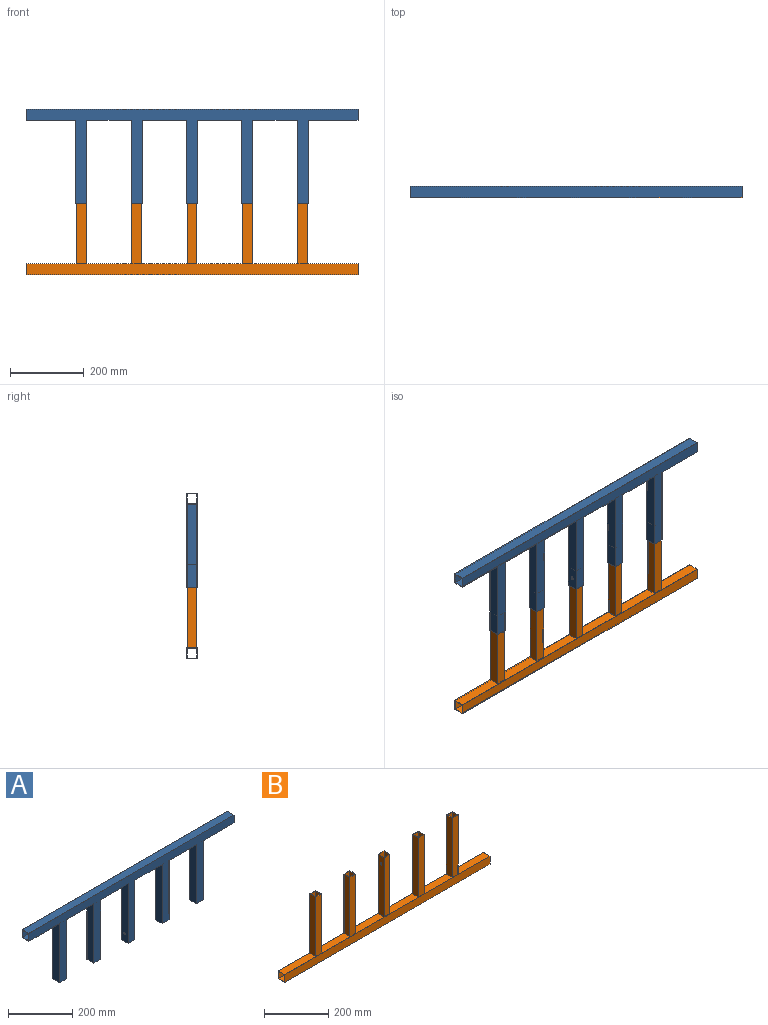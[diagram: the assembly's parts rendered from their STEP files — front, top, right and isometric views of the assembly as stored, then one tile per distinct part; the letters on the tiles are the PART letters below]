
ASSEMBLY  parts=2 mates=1
PART A: 57 faces, bbox 900x30x255 mm
  f0: plane 120x30mm, normal (0,0,-1), area 3600mm2, adj f13,f14,f39,f52
  f1: plane 135x30mm, normal (0,0,-1), area 4050mm2, adj f9,f13,f14,f47
  f2: plane 120x30mm, normal (0,0,-1), area 3600mm2, adj f13,f14,f15,f44
  f3: plane 120x30mm, normal (0,0,-1), area 3600mm2, adj f13,f14,f23,f36
  f4: plane 120x30mm, normal (0,0,-1), area 3600mm2, adj f13,f14,f20,f31
  f5: plane 135x30mm, normal (0,0,-1), area 4050mm2, adj f6,f13,f14,f28
  f6: plane 30x30mm, normal (1,0,0), area 224mm2, adj f5,f7,f8,f10,f11,f12,f13,f14
  f7: plane 900x26mm, normal (0,-1,0), area 23400mm2, adj f6,f9,f10,f11
  f8: plane 900x30mm, normal (0,0,1), area 27000mm2, adj f6,f9,f13,f14
  f9: plane 30x30mm, normal (-1,0,0), area 224mm2, adj f1,f7,f8,f10,f11,f12,f13,f14
  f10: plane 900x26mm, normal (0,0,1), area 23400mm2, adj f6,f7,f9,f12
  f11: plane 900x26mm, normal (0,0,-1), area 23400mm2, adj f6,f7,f9,f12
  f12: plane 900x26mm, normal (0,1,0), area 23400mm2, adj f6,f9,f10,f11
  f13: plane 900x255mm, normal (0,-1,0), area 60750mm2, adj f0,f1,f2,f3,f4,f5,f6,f8
  f14: plane 900x255mm, normal (0,1,0), area 60750mm2, adj f0,f1,f2,f3,f4,f5,f6,f8
  f15: plane 225x30mm, normal (-1,0,0), area 6699.7mm2, adj f2,f13,f14,f21,f56
  f16: plane 225x26mm, normal (1,0,0), area 5799.7mm2, adj f17,f19,f21,f22,f56
  f17: plane 225x26mm, normal (0,1,0), area 5850mm2, adj f16,f18,f21,f22
  f18: plane 225x26mm, normal (-1,0,0), area 5799.7mm2, adj f17,f19,f21,f22,f55
  f19: plane 225x26mm, normal (0,-1,0), area 5850mm2, adj f16,f18,f21,f22
  f20: plane 225x30mm, normal (1,0,0), area 6699.7mm2, adj f4,f13,f14,f21,f55
  f21: plane 30x30mm, normal (0,0,-1), area 224mm2, adj f13,f14,f15,f16,f17,f18,f19,f20
  f22: plane 26x26mm, normal (0,0,-1), area 676mm2, adj f16,f17,f18,f19
  f23: plane 225x30mm, normal (-1,0,0), area 6750mm2, adj f3,f13,f14,f29
  f24: plane 225x26mm, normal (1,0,0), area 5850mm2, adj f25,f27,f29,f30
  f25: plane 225x26mm, normal (0,1,0), area 5850mm2, adj f24,f26,f29,f30
  f26: plane 225x26mm, normal (-1,0,0), area 5850mm2, adj f25,f27,f29,f30
  f27: plane 225x26mm, normal (0,-1,0), area 5850mm2, adj f24,f26,f29,f30
  f28: plane 225x30mm, normal (1,0,0), area 6750mm2, adj f5,f13,f14,f29
  f29: plane 30x30mm, normal (0,0,-1), area 224mm2, adj f13,f14,f23,f24,f25,f26,f27,f28
  f30: plane 26x26mm, normal (0,0,-1), area 676mm2, adj f24,f25,f26,f27
  f31: plane 225x30mm, normal (-1,0,0), area 6750mm2, adj f4,f13,f14,f37
  f32: plane 225x26mm, normal (1,0,0), area 5850mm2, adj f33,f35,f37,f38
  f33: plane 225x26mm, normal (0,1,0), area 5850mm2, adj f32,f34,f37,f38
  f34: plane 225x26mm, normal (-1,0,0), area 5850mm2, adj f33,f35,f37,f38
  f35: plane 225x26mm, normal (0,-1,0), area 5850mm2, adj f32,f34,f37,f38
  f36: plane 225x30mm, normal (1,0,0), area 6750mm2, adj f3,f13,f14,f37
  f37: plane 30x30mm, normal (0,0,-1), area 224mm2, adj f13,f14,f31,f32,f33,f34,f35,f36
  f38: plane 26x26mm, normal (0,0,-1), area 676mm2, adj f32,f33,f34,f35
  f39: plane 225x30mm, normal (-1,0,0), area 6750mm2, adj f0,f13,f14,f45
  f40: plane 225x26mm, normal (1,0,0), area 5850mm2, adj f41,f43,f45,f46
  f41: plane 225x26mm, normal (0,1,0), area 5850mm2, adj f40,f42,f45,f46
  f42: plane 225x26mm, normal (-1,0,0), area 5850mm2, adj f41,f43,f45,f46
  f43: plane 225x26mm, normal (0,-1,0), area 5850mm2, adj f40,f42,f45,f46
  f44: plane 225x30mm, normal (1,0,0), area 6750mm2, adj f2,f13,f14,f45
  f45: plane 30x30mm, normal (0,0,-1), area 224mm2, adj f13,f14,f39,f40,f41,f42,f43,f44
  f46: plane 26x26mm, normal (0,0,-1), area 676mm2, adj f40,f41,f42,f43
  f47: plane 225x30mm, normal (-1,0,0), area 6750mm2, adj f1,f13,f14,f53
  f48: plane 225x26mm, normal (1,0,0), area 5850mm2, adj f49,f51,f53,f54
  f49: plane 225x26mm, normal (0,1,0), area 5850mm2, adj f48,f50,f53,f54
  f50: plane 225x26mm, normal (-1,0,0), area 5850mm2, adj f49,f51,f53,f54
  f51: plane 225x26mm, normal (0,-1,0), area 5850mm2, adj f48,f50,f53,f54
  f52: plane 225x30mm, normal (1,0,0), area 6750mm2, adj f0,f13,f14,f53
  f53: plane 30x30mm, normal (0,0,-1), area 224mm2, adj f13,f14,f47,f48,f49,f50,f51,f52
  f54: plane 26x26mm, normal (0,0,-1), area 676mm2, adj f48,f49,f50,f51
  f55: cylinder r=4mm len=8mm, axis (-1,0,0), area 50.3mm2, adj f18,f20
  f56: cylinder r=4mm len=8mm, axis (-1,0,0), area 50.3mm2, adj f15,f16
PART B: 62 faces, bbox 900x30x255 mm
  f0: plane 22x22mm, normal (0,0,1), area 484mm2, adj f8,f9,f10,f11
  f1: plane 22x22mm, normal (0,0,1), area 484mm2, adj f17,f18,f19,f20
  f2: plane 22x22mm, normal (0,0,1), area 484mm2, adj f26,f27,f28,f29
  f3: plane 22x22mm, normal (0,0,1), area 484mm2, adj f35,f36,f37,f38
  f4: plane 225x26mm, normal (0,1,0), area 5850mm2, adj f5,f7,f12,f40
  f5: plane 225x26mm, normal (-1,0,0), area 5850mm2, adj f4,f6,f12,f40
  f6: plane 225x26mm, normal (0,-1,0), area 5850mm2, adj f5,f7,f12,f40
  f7: plane 225x26mm, normal (1,0,0), area 5850mm2, adj f4,f6,f12,f40
  f8: plane 225x22mm, normal (1,0,0), area 4950mm2, adj f0,f9,f11,f12
  f9: plane 225x22mm, normal (0,-1,0), area 4950mm2, adj f0,f8,f10,f12
  f10: plane 225x22mm, normal (-1,0,0), area 4950mm2, adj f0,f9,f11,f12
  f11: plane 225x22mm, normal (0,1,0), area 4950mm2, adj f0,f8,f10,f12
  f12: plane 26x26mm, normal (0,0,1), area 192mm2, adj f4,f5,f6,f7,f8,f9,f10,f11
  f13: plane 225x26mm, normal (0,1,0), area 5850mm2, adj f14,f16,f21,f40
  f14: plane 225x26mm, normal (-1,0,0), area 5850mm2, adj f13,f15,f21,f40
  f15: plane 225x26mm, normal (0,-1,0), area 5850mm2, adj f14,f16,f21,f40
  f16: plane 225x26mm, normal (1,0,0), area 5850mm2, adj f13,f15,f21,f40
  f17: plane 225x22mm, normal (1,0,0), area 4950mm2, adj f1,f18,f20,f21
  f18: plane 225x22mm, normal (0,-1,0), area 4950mm2, adj f1,f17,f19,f21
  f19: plane 225x22mm, normal (-1,0,0), area 4950mm2, adj f1,f18,f20,f21
  f20: plane 225x22mm, normal (0,1,0), area 4950mm2, adj f1,f17,f19,f21
  f21: plane 26x26mm, normal (0,0,1), area 192mm2, adj f13,f14,f15,f16,f17,f18,f19,f20
  f22: plane 225x26mm, normal (0,1,0), area 5850mm2, adj f23,f25,f30,f40
  f23: plane 225x26mm, normal (-1,0,0), area 5850mm2, adj f22,f24,f30,f40
  f24: plane 225x26mm, normal (0,-1,0), area 5850mm2, adj f23,f25,f30,f40
  f25: plane 225x26mm, normal (1,0,0), area 5850mm2, adj f22,f24,f30,f40
  f26: plane 225x22mm, normal (1,0,0), area 4950mm2, adj f2,f27,f29,f30
  f27: plane 225x22mm, normal (0,-1,0), area 4950mm2, adj f2,f26,f28,f30
  f28: plane 225x22mm, normal (-1,0,0), area 4950mm2, adj f2,f27,f29,f30
  f29: plane 225x22mm, normal (0,1,0), area 4950mm2, adj f2,f26,f28,f30
  f30: plane 26x26mm, normal (0,0,1), area 192mm2, adj f22,f23,f24,f25,f26,f27,f28,f29
  f31: plane 225x26mm, normal (0,1,0), area 5850mm2, adj f32,f34,f39,f40
  f32: plane 225x26mm, normal (-1,0,0), area 5850mm2, adj f31,f33,f39,f40
  f33: plane 225x26mm, normal (0,-1,0), area 5850mm2, adj f32,f34,f39,f40
  f34: plane 225x26mm, normal (1,0,0), area 5850mm2, adj f31,f33,f39,f40
  f35: plane 225x22mm, normal (1,0,0), area 4950mm2, adj f3,f36,f38,f39
  f36: plane 225x22mm, normal (0,-1,0), area 4950mm2, adj f3,f35,f37,f39
  f37: plane 225x22mm, normal (-1,0,0), area 4950mm2, adj f3,f36,f38,f39
  f38: plane 225x22mm, normal (0,1,0), area 4950mm2, adj f3,f35,f37,f39
  f39: plane 26x26mm, normal (0,0,1), area 192mm2, adj f31,f32,f33,f34,f35,f36,f37,f38
  f40: plane 900x30mm, normal (0,0,1), area 23620mm2, adj f4,f5,f6,f7,f13,f14,f15,f16
  f41: plane 30x30mm, normal (1,0,0), area 224mm2, adj f40,f42,f44,f45,f46,f47,f48,f49
  f42: plane 900x26mm, normal (0,-1,0), area 23400mm2, adj f41,f43,f44,f45
  f43: plane 30x30mm, normal (-1,0,0), area 224mm2, adj f40,f42,f44,f45,f46,f47,f48,f49
  f44: plane 900x26mm, normal (0,0,1), area 23400mm2, adj f41,f42,f43,f46
  f45: plane 900x26mm, normal (0,0,-1), area 23400mm2, adj f41,f42,f43,f46
  f46: plane 900x26mm, normal (0,1,0), area 23400mm2, adj f41,f43,f44,f45
  f47: plane 900x30mm, normal (0,-1,0), area 27000mm2, adj f40,f41,f43,f49
  f48: plane 900x30mm, normal (0,1,0), area 27000mm2, adj f40,f41,f43,f49
  f49: plane 900x30mm, normal (0,0,-1), area 27000mm2, adj f41,f43,f47,f48
  f50: plane 225x22mm, normal (1,0,0), area 4899.7mm2, adj f51,f57,f58,f59,f61
  f51: plane 225x22mm, normal (0,-1,0), area 4950mm2, adj f50,f52,f58,f59
  f52: plane 225x22mm, normal (-1,0,0), area 4899.7mm2, adj f51,f57,f58,f59,f60
  f53: plane 225x26mm, normal (0,1,0), area 5850mm2, adj f40,f54,f56,f58
  f54: plane 225x26mm, normal (-1,0,0), area 5799.7mm2, adj f40,f53,f55,f58,f61
  f55: plane 225x26mm, normal (0,-1,0), area 5850mm2, adj f40,f54,f56,f58
  f56: plane 225x26mm, normal (1,0,0), area 5799.7mm2, adj f40,f53,f55,f58,f60
  f57: plane 225x22mm, normal (0,1,0), area 4950mm2, adj f50,f52,f58,f59
  f58: plane 26x26mm, normal (0,0,1), area 192mm2, adj f50,f51,f52,f53,f54,f55,f56,f57
  f59: plane 22x22mm, normal (0,0,1), area 484mm2, adj f50,f51,f52,f57
  f60: cylinder r=4mm len=8mm, axis (-1,0,0), area 50.3mm2, adj f52,f56
  f61: cylinder r=4mm len=8mm, axis (-1,0,0), area 50.3mm2, adj f50,f54
PLACE A t=(-150.85,-78.55,-9.68)mm
PLACE B t=(-150.85,-78.55,-9.68)mm fixed
MATE slider B.f40 <-> A.f53  axis (0,0,-1) through (-463.85,-80.55,-204.68)mm
